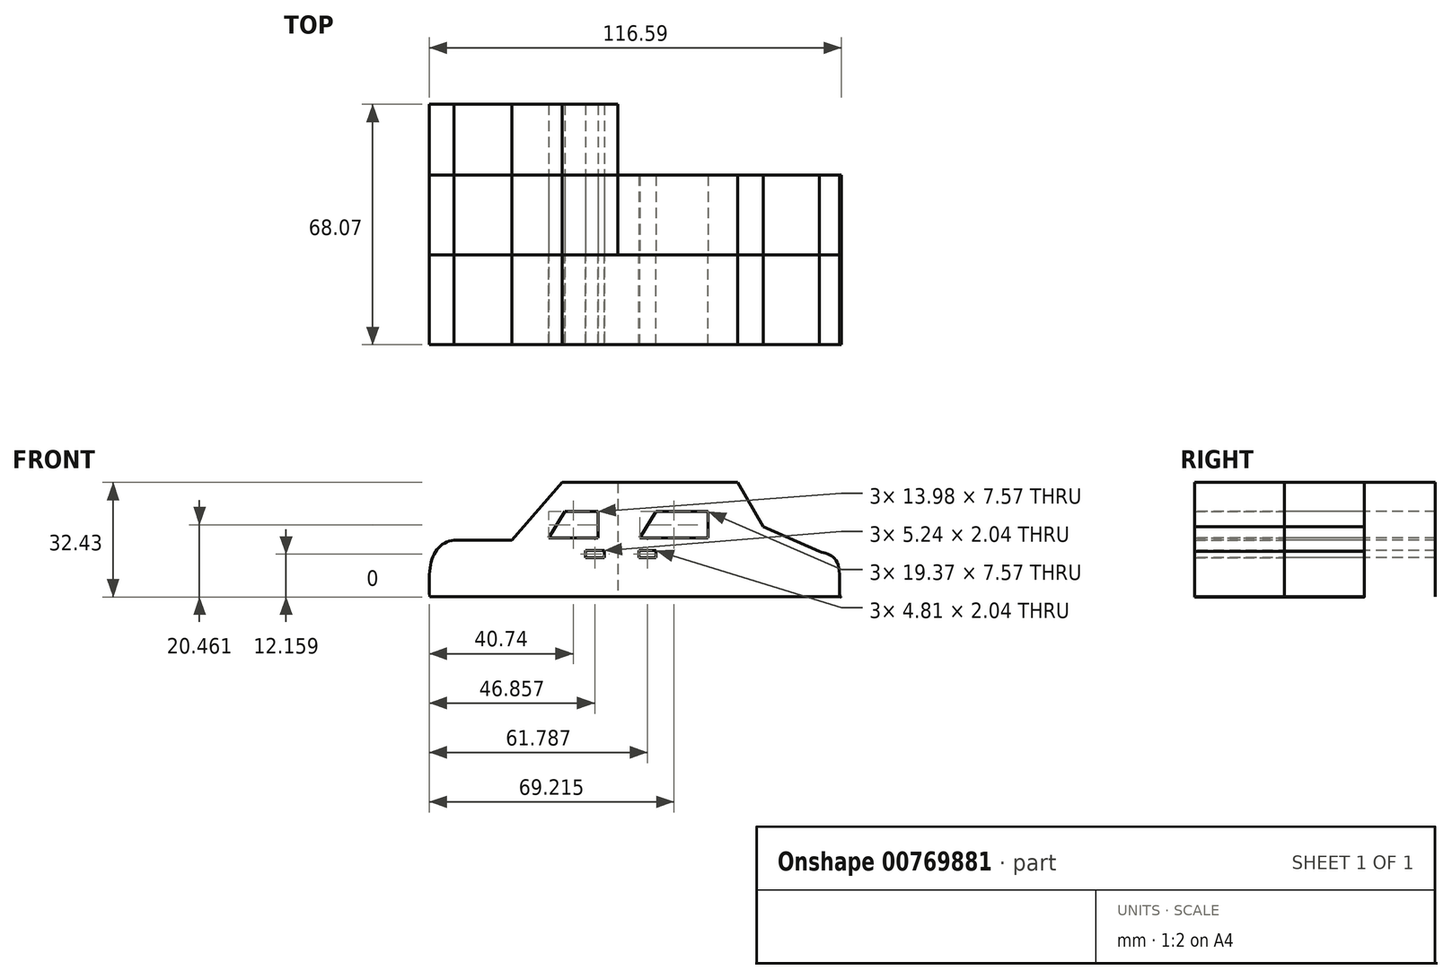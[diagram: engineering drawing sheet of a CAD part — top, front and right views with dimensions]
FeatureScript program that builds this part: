
annotation { "Feature Type Name" : "Feature", "Feature Type Description" : "" }
export const myFeature = defineFeature(function(context is Context, id is Id, definition is map)
    precondition{}
    {
        {
            var Q0;
            Q0=qCreatedBy(makeId("Front.planeOp"),FACE);
            var sketch = newSketch(context, id + "F0", { "sketchPlane" : qUnion([Q0])});
            skLineSegment(sketch, "E0", {"start": v(-57.15, 16.05) * mm, "end": v(-40.84, 16.05) * mm});
            skFitSpline(sketch, "E1", {"points": [v(-57.15, 16.05) * mm, v(-62.74, 12.23) * mm, v(-64.08, 0) * mm], "startDerivative": vector(-16.43, -1.77) * mm, "endDerivative": vector(1.14, -25.53) * mm});
            skLineSegment(sketch, "E2", {"start": v(-26.6, 32.36) * mm, "end": v(-10.89, 32.36) * mm});
            skLineSegment(sketch, "E3", {"start": v(-10.89, 32.36) * mm, "end": v(23.07, 32.36) * mm});
            skLineSegment(sketch, "E4", {"start": v(30.29, 19.8) * mm, "end": v(46.21, 12.84) * mm});
            skFitSpline(sketch, "E5", {"points": [v(46.21, 12.84) * mm, v(51.26, 9.67) * mm, v(52.08, 0) * mm, v(52.4, 0) * mm], "startDerivative": vector(15.37, -4.9) * mm, "endDerivative": vector(3.96, 1.92) * mm});
            skLineSegment(sketch, "E6", {"start": v(52.4, 0) * mm, "end": v(31.58, 0) * mm});
            skLineSegment(sketch, "E7", {"start": v(-64.08, 0) * mm, "end": v(-40.84, 0) * mm});
            skLineSegment(sketch, "E8", {"start": v(-46.52, 0) * mm, "end": v(0, 0) * mm});
            skPoint(sketch, "E9.endSnap0", {"position": v(18.83, 16.05) * mm});
            skLineSegment(sketch, "E10", {"start": v(14.71, 24.18) * mm, "end": v(0, 24.18) * mm});
            skLineSegment(sketch, "E11", {"start": v(0, 24.18) * mm, "end": v(-4.66, 16.6) * mm});
            skLineSegment(sketch, "E12", {"start": v(-4.66, 16.6) * mm, "end": v(14.71, 16.6) * mm});
            skLineSegment(sketch, "E13", {"start": v(14.71, 16.6) * mm, "end": v(14.71, 24.18) * mm});
            skLineSegment(sketch, "E14.bottom", {"start": v(-14.71, 13.1) * mm, "end": v(-19.95, 13.1) * mm});
            skLineSegment(sketch, "E14.top", {"start": v(-14.71, 11.07) * mm, "end": v(-19.95, 11.07) * mm});
            skLineSegment(sketch, "E14.left", {"start": v(-14.71, 13.1) * mm, "end": v(-14.71, 11.07) * mm});
            skLineSegment(sketch, "E14.right", {"start": v(-19.95, 13.1) * mm, "end": v(-19.95, 11.07) * mm});
            skLineSegment(sketch, "E15.bottom", {"start": v(-4.8, 11.07) * mm, "end": v(0, 11.07) * mm});
            skLineSegment(sketch, "E15.top", {"start": v(-4.8, 13.1) * mm, "end": v(0, 13.1) * mm});
            skLineSegment(sketch, "E15.left", {"start": v(-4.8, 11.07) * mm, "end": v(-4.8, 13.1) * mm});
            skLineSegment(sketch, "E15.right", {"start": v(0, 11.07) * mm, "end": v(0, 13.1) * mm});
            skPoint(sketch, "E16.end.orphan", {"position": v(-25.78, 24.18) * mm});
            skPoint(sketch, "E17.start.orphan", {"position": v(-30.44, 16.6) * mm});
            skPoint(sketch, "E9.end.orphan", {"position": v(-41.22, 16.05) * mm});
            skLineSegment(sketch, "E18", {"start": v(-25.78, 24.18) * mm, "end": v(-30.44, 16.6) * mm});
            skLineSegment(sketch, "E19", {"start": v(-30.44, 16.6) * mm, "end": v(-16.46, 16.6) * mm});
            skLineSegment(sketch, "E20", {"start": v(-16.46, 16.6) * mm, "end": v(-16.46, 24.18) * mm});
            skLineSegment(sketch, "E21", {"start": v(18.83, 0) * mm, "end": v(18.83, 0) * mm});
            skPoint(sketch, "E22.start.orphan", {"position": v(-10.89, 27.1) * mm});
            skLineSegment(sketch, "E23", {"start": v(-40.84, 16.05) * mm, "end": v(-26.6, 32.36) * mm});
            skLineSegment(sketch, "E24", {"start": v(30.29, 19.8) * mm, "end": v(23.07, 32.36) * mm});
            skLineSegment(sketch, "E25", {"start": v(-10.89, 32.36) * mm, "end": v(-10.89, 0) * mm});
            skLineSegment(sketch, "E26", {"start": v(-64.08, 0) * mm, "end": v(-46.52, 0) * mm});
            skPoint(sketch, "E27.end.orphan", {"position": v(42, 0) * mm});
            skPoint(sketch, "E28.start.orphan", {"position": v(-52.46, 0) * mm});
            skPoint(sketch, "E29.oppositeSnap0", {"position": v(-23.45, 16.6) * mm});
            skPoint(sketch, "E29.oppositeSnap1", {"position": v(-28.11, 20.4) * mm});
            skPoint(sketch, "E30.trimOffspring.end.orphan", {"position": v(-23.45, 20.4) * mm});
            skLineSegment(sketch, "E31", {"start": v(-16.46, 24.18) * mm, "end": v(-25.78, 24.18) * mm});
            skLineSegment(sketch, "E32.trimOffspring", {"start": v(-28.37, 0) * mm, "end": v(31.58, 0) * mm});
            skSolve(sketch);
        }
        {
            var Q0;
            Q0=makeQuery(id+"F0.imprint","IMPRINT",FACE,{"disambiguationData":[TD([[makeQuery(id+"F0.imprint","IMPRINT",EDGE,{"derivedFrom":sQuery(id+"F0.wireOp",EDGE,"E0")}),-1.0]])]});
            extrude(context, id + "F1", {"entities" : qUnion([Q0]), "oppositeDirection" : true, "depth" : 42.67 * mm, "offsetDistance" : 25.4 * mm});
        }
        {
            var Q0;
            Q0 = qSketchRegion(id + "F0", true);
            extrude(context, id + "F2", {"entities" : qUnion([Q0]), "operationType" : NewBodyOperationType.ADD, "depth" : 25.4 * mm, "offsetDistance" : 25.4 * mm});
        }
        {
            var Q0;
            Q0 = qSketchRegion(id + "F0", true);
            extrude(context, id + "F3", {"entities" : qUnion([Q0]), "depth" : 25.4 * mm, "offsetDistance" : 25.4 * mm});
        }
        {
            var Q0;
            Q0 = qSketchRegion(id + "F0", true);
            extrude(context, id + "F4", {"entities" : qUnion([Q0]), "oppositeDirection" : true, "depth" : 22.6 * mm, "offsetDistance" : 25.4 * mm});
        }
    });
